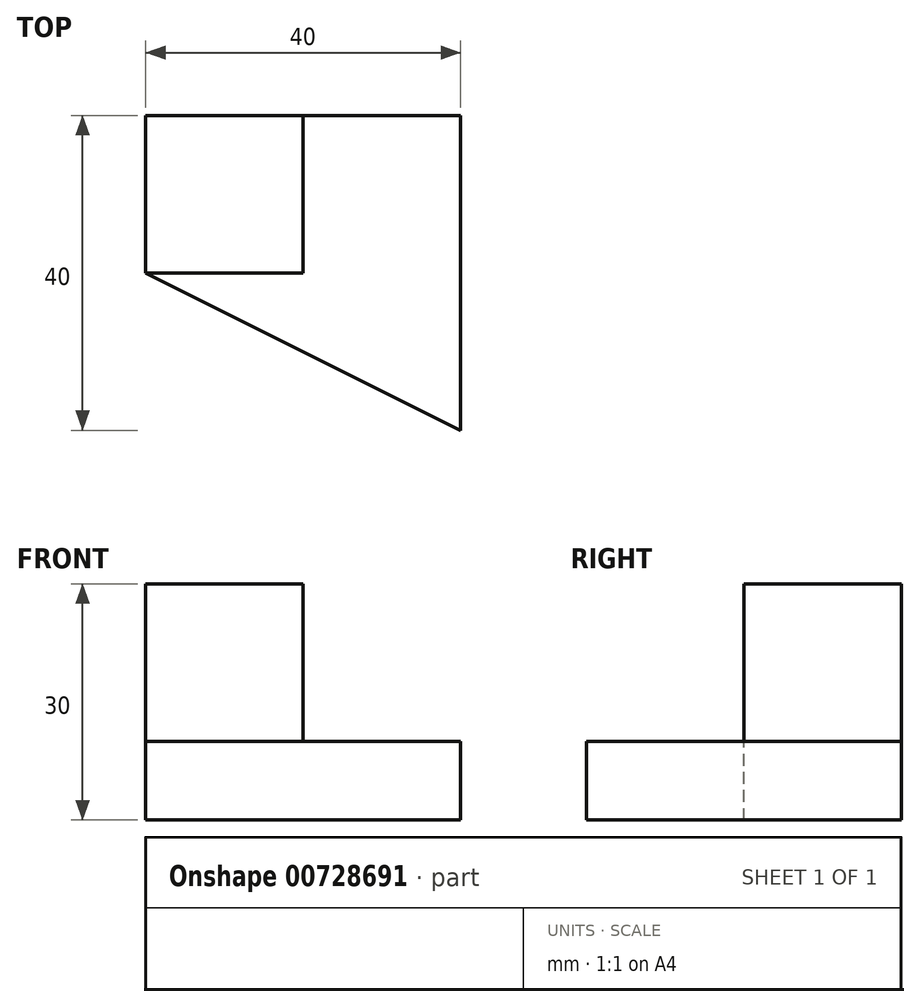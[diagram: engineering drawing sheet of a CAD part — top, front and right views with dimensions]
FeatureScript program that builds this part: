
annotation { "Feature Type Name" : "Feature", "Feature Type Description" : "" }
export const myFeature = defineFeature(function(context is Context, id is Id, definition is map)
    precondition{}
    {
        {
            var Q0;
            Q0=qCreatedBy(makeId("Top.planeOp"),FACE);
            var sketch = newSketch(context, id + "F0", { "sketchPlane" : qUnion([Q0])});
            skLineSegment(sketch, "E0.bottom", {"start": v(-18.44, -21.38) * mm, "end": v(21.56, -21.38) * mm});
            skLineSegment(sketch, "E0.top", {"start": v(-18.44, 18.62) * mm, "end": v(21.56, 18.62) * mm});
            skLineSegment(sketch, "E0.left", {"start": v(-18.44, -21.38) * mm, "end": v(-18.44, 18.62) * mm});
            skLineSegment(sketch, "E0.right", {"start": v(21.56, -21.38) * mm, "end": v(21.56, 18.62) * mm});
            skSolve(sketch);
        }
        {
            var Q0;
            Q0=makeQuery(id+"F0.imprint","IMPRINT",FACE,{"disambiguationData":[TD([[makeQuery(id+"F0.imprint","IMPRINT",EDGE,{"derivedFrom":sQuery(id+"F0.wireOp",EDGE,"E0.bottom")}),1.0]])]});
            extrude(context, id + "F1", {"entities" : qUnion([Q0]), "depth" : 10 * mm, "offsetDistance" : 25 * mm});
        }
        {
            var Q0;
            Q0=makeQuery(id+"F1.opExtrude","CAP_FACE",FACE,{"disambiguationData":[OSD([sQuery(id+"F0.wireOp",EDGE,"E0.bottom"),sQuery(id+"F0.wireOp",EDGE,"E0.top"),sQuery(id+"F0.wireOp",EDGE,"E0.left"),sQuery(id+"F0.wireOp",EDGE,"E0.right")])],"isStart":false});
            var sketch = newSketch(context, id + "F2", { "sketchPlane" : qUnion([Q0])});
            skLineSegment(sketch, "E1", {"start": v(-18.44, -1.38) * mm, "end": v(21.56, -21.38) * mm});
            skLineSegment(sketch, "E2", {"start": v(21.56, -21.38) * mm, "end": v(-18.44, -21.38) * mm});
            skLineSegment(sketch, "E3", {"start": v(-18.44, -21.38) * mm, "end": v(-18.44, -1.38) * mm});
            skSolve(sketch);
        }
        {
            var Q0;
            Q0=makeQuery(id+"F2.imprint","IMPRINT",FACE,{"disambiguationData":[TD([[makeQuery(id+"F2.imprint","IMPRINT",EDGE,{"derivedFrom":sQuery(id+"F2.wireOp",EDGE,"E1")}),-1.0]])]});
            extrude(context, id + "F3", {"entities" : qUnion([Q0]), "operationType" : NewBodyOperationType.REMOVE, "oppositeDirection" : true, "depth" : 10 * mm, "offsetDistance" : 25 * mm});
        }
        {
            var Q0;
            Q0=makeQuery(id+"F1.opExtrude","CAP_FACE",FACE,{"disambiguationData":[OSD([sQuery(id+"F0.wireOp",EDGE,"E0.bottom"),sQuery(id+"F0.wireOp",EDGE,"E0.top"),sQuery(id+"F0.wireOp",EDGE,"E0.left"),sQuery(id+"F0.wireOp",EDGE,"E0.right")])],"isStart":false});
            var sketch = newSketch(context, id + "F4", { "sketchPlane" : qUnion([Q0])});
            skLineSegment(sketch, "E4.bottom", {"start": v(-18.44, 18.62) * mm, "end": v(1.56, 18.62) * mm});
            skLineSegment(sketch, "E4.top", {"start": v(-18.44, -1.38) * mm, "end": v(1.56, -1.38) * mm});
            skLineSegment(sketch, "E4.left", {"start": v(-18.44, 18.62) * mm, "end": v(-18.44, -1.38) * mm});
            skLineSegment(sketch, "E4.right", {"start": v(1.56, 18.62) * mm, "end": v(1.56, -1.38) * mm});
            skSolve(sketch);
        }
        {
            var Q0;
            Q0=makeQuery(id+"F4.imprint","IMPRINT",FACE,{"disambiguationData":[TD([[makeQuery(id+"F4.imprint","IMPRINT",EDGE,{"derivedFrom":sQuery(id+"F4.wireOp",EDGE,"E4.bottom")}),-1.0]])]});
            extrude(context, id + "F5", {"entities" : qUnion([Q0]), "operationType" : NewBodyOperationType.ADD, "depth" : 20 * mm, "offsetDistance" : 25 * mm});
        }
    });
